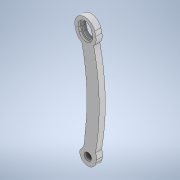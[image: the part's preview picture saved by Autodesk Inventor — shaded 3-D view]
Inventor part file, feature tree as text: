
AUTODESK INVENTOR PART (.ipt)
format: ipt  version: 2020.3 (Build 243373000, 373)  size: 232,448 bytes
history: native  units: mm
features: extrude x8, sketch x6, projected_geometry x6, plane x4, other x3
ambient origin geometry x8: Origin, YZ Plane, XZ Plane, XY Plane, X Axis, Y Axis, Z Axis, Center Point
bodies: Solid1 (feature_tree)
feature tree (27):
  plane  "Work Plane1"
  plane  "Work Plane3"
  extrude  "Extrusion2"  Depth=3.0mm TaperAngle=0.0deg
  plane  "Work Plane6"
  extrude  "Extrusion4"  Depth=5.0mm TaperAngle=0.0deg
  plane  "Work Plane7"
  extrude  "Extrusion5"  Depth=10.0mm
  sketch  "Sketch7"  dims[d20=8.0mm d21=1.5mm]
  extrude  "Extrusion6"  Depth=1.5mm
  extrude  "Extrusion7"  Depth=5.0mm TaperAngle=0.0deg
  sketch  "Sketch8"  dims[d22=10.0mm d23=0.0mm d24=5.0mm d25=0.0mm]
  extrude  "Extrusion8"  Depth=1.0mm
  extrude  "Extrusion9"  Depth=10.0mm TaperAngle=0.0deg
  extrude  "Extrusion10"  Depth=2.5mm
  sketch  "Sketch2"  dims[d4=3.0mm d5=0.0mm d10=3.0mm d11=0.0mm]
  projected_geometry  "Projected Loop1"
  projected_geometry  "Projected Loop2"
  sketch  "Sketch4"  dims[d12=3.5mm d13=5.0mm d14=0.0mm]
  projected_geometry  "Projected Loop3"
  projected_geometry  "Projected Loop4"
  sketch  "Sketch5"  dims[d16=10.0mm d19=3.6mm]
  projected_geometry  "Projected Loop6"
  sketch  "Sketch9"  dims[d26=1.0mm d27=1.0mm d29=10.0mm d30=0.0mm d31=2.5mm d32=0.8mm d33=1.0mm d34=0.0mm d35=10.0mm d36=0.0mm]
  projected_geometry  "Projected Loop7"
  parser-record x1  (decoder bookkeeping rows leaked as tree rows — omitted from the tree; the rows remain in map.json)
  other  "kez.iam"
  other  "motortarcsa:2"
note: 1 file-system path scrubbed to <path> (originals preserved in map.json)
